# Revit family: RN 80051 Optipress-Aquaplus-Flanschübergang PN 16
name_source: partatom
category: Rohrformteile
units: mm (PartAtom-declared; Revit-internal decimal feet)

## family parameters
Arbeitsebenenbasiert = Nein
Beim Laden mit Abzugskörper schneiden = Nein
Bemaßung runder Anschluss = Durchmesser verwenden
Gemeinsam genutzt = Nein
Immer vertikal = Ja
Teiletyp = Verbindung

## types (6) — shared parameters
1.010.00.2 Blattnummer der Richtlinie = 29
1.010.00.3 Ausgabedatum (Monat) der Richtlinie = 201308
1.010.00.4 Herstellername = R. Nussbaum AG
1.010.00.5 Revisionsdatum der Datei = 20190521
1.010.00.6 Webadresse des Herstellers = http://www.nussbaum.ch
1.100.00.4 Produktbezeichnung = Versorgung
1.110.00.2 Index = 4
1.110.00.4 Produktbezeichnung = Optipress
1.960/3L.00.8 Link (URL) = https://www.nussbaum.ch
29.700.00.4 Produktname = Optipress-Aquaplus-Flanschübergang PN 16, mit Einsteckende
29.700.00.5 Produktkennung = 2
29.700.00.6 Querschnittsform = 1
29.700.00.7 Nennweitensystem = DN
29.700.00.8 Nenndrucksystem = PN
29.710.02.4 Nenndruck = 16
29.710.02.5 max. zul. Überdruck [hPa] = 1600
29.710.02.7 max. zul. Dauer-Betriebsdruck [hPa] = 1600
29.710.02.9 max. zul. Dauer-Betriebstemperatur [°C] = 95
CONNECTOR0_dX_00 = 1 mm  [stored 0.00328084 ft]
CONNECTOR0_ref_dX = 1 mm  [stored 0.00328084 ft]
Connector Visibility = Nein
EnclosingSpace Visibility = Nein

## per-type parameters (varying)
| type | 1.800.00.3 TGA-Nummer | 1.810.00.3 Hersteller-Bestellnummer | 1.810.00.4 DATANORM-Nummer | 1.810.00.5 StLB-Nummer | 1.810.00.6 GTIN-Nummer | 29.710.02.10 Formstück-Gewicht [kg] | 29.710.02.3 Benennung | CONNECTOR0_DIAMETER_dX_0r | CONNECTOR1_DIAMETER_dX_0r | CONNECTOR1_dX_00 | CONNECTOR1_dX_01 | CONNECTOR1_ref_dX | R. Nussbaum AG 80051.27 de Visibility | R. Nussbaum AG 80051.28 de Visibility | R. Nussbaum AG 80051.69 de Visibility | R. Nussbaum AG 80051.71 de Visibility | R. Nussbaum AG 80051.72 de Visibility | R. Nussbaum AG 80051.73 de Visibility |
| 80051.27, Optipress-Aquaplus-Flanschübergang PN 16, mit Einsteckende, DN=40 | 01900400000000000000000000000000000000000000000033000000000000000001 | 80051.27 | 80051.27 | 267.177 | 7612945709332 | 1.665 | Optipress-Aquaplus-Flanschübergang PN 16, mit Einsteckende, DN=40 | 40 mm | 40 mm | 69 mm | 105 mm | 69 mm | Ja | Nein | Nein | Nein | Nein | Nein |
| 80051.28, Optipress-Aquaplus-Flanschübergang PN 16, mit Einsteckende, DN=50 | 01900400000000000000000000000000000000000000000033000000000000000002 | 80051.28 | 80051.28 | 267.178 | 7612945709349 | 1.959 | Optipress-Aquaplus-Flanschübergang PN 16, mit Einsteckende, DN=50 | 50 mm | 50 mm | 83 mm | 123 mm | 83 mm | Nein | Ja | Nein | Nein | Nein | Nein |
| 80051.69, Optipress-Aquaplus-Flanschübergang PN 16, mit Einsteckende, DN=60 | 01900400000000000000000000000000000000000000000033000000000000000003 | 80051.69 | 80051.69 | 267.184 | 7612945692849 | 2.639 | Optipress-Aquaplus-Flanschübergang PN 16, mit Einsteckende, DN=60 | 50 mm | 60 mm | 76 mm | 119 mm | 76 mm | Nein | Nein | Ja | Nein | Nein | Nein |
| 80051.71, Optipress-Aquaplus-Flanschübergang PN 16, mit Einsteckende, DN=65 | 01900400000000000000000000000000000000000000000033000000000000000004 | 80051.71 | 80051.71 | 267.181 | 7612945692856 | 2.909 | Optipress-Aquaplus-Flanschübergang PN 16, mit Einsteckende, DN=65 | 65 mm | 65 mm | 83 mm | 133 mm | 83 mm | Nein | Nein | Nein | Ja | Nein | Nein |
| 80051.72, Optipress-Aquaplus-Flanschübergang PN 16, mit Einsteckende, DN=80 | 01900400000000000000000000000000000000000000000033000000000000000005 | 80051.72 | 80051.72 | 267.182 | 7612945692863 | 3.999 | Optipress-Aquaplus-Flanschübergang PN 16, mit Einsteckende, DN=80 | 80 mm | 80 mm | 85 mm | 135 mm | 85 mm | Nein | Nein | Nein | Nein | Ja | Nein |
| 80051.73, Optipress-Aquaplus-Flanschübergang PN 16, mit Einsteckende, DN=100 | 01900400000000000000000000000000000000000000000033000000000000000006 | 80051.73 | 80051.73 | 267.183 | 7612945692870 | 4.749 | Optipress-Aquaplus-Flanschübergang PN 16, mit Einsteckende, DN=100 | 100 mm  [stored 0.328084 ft] | 100 mm  [stored 0.328084 ft] | 95 mm | 155 mm | 95 mm | Nein | Nein | Nein | Nein | Nein | Ja |

note: column(s) folded — value = type name in every type: 1.800.00.4 Kommentarfeld

note: [stored X ft] marks values corroborated as IEEE doubles in the binary element streams (Revit-internal decimal feet)

## geometry (parser evidence)
native form markers: Sweep x2
no freeform markers — native parametric forms only
